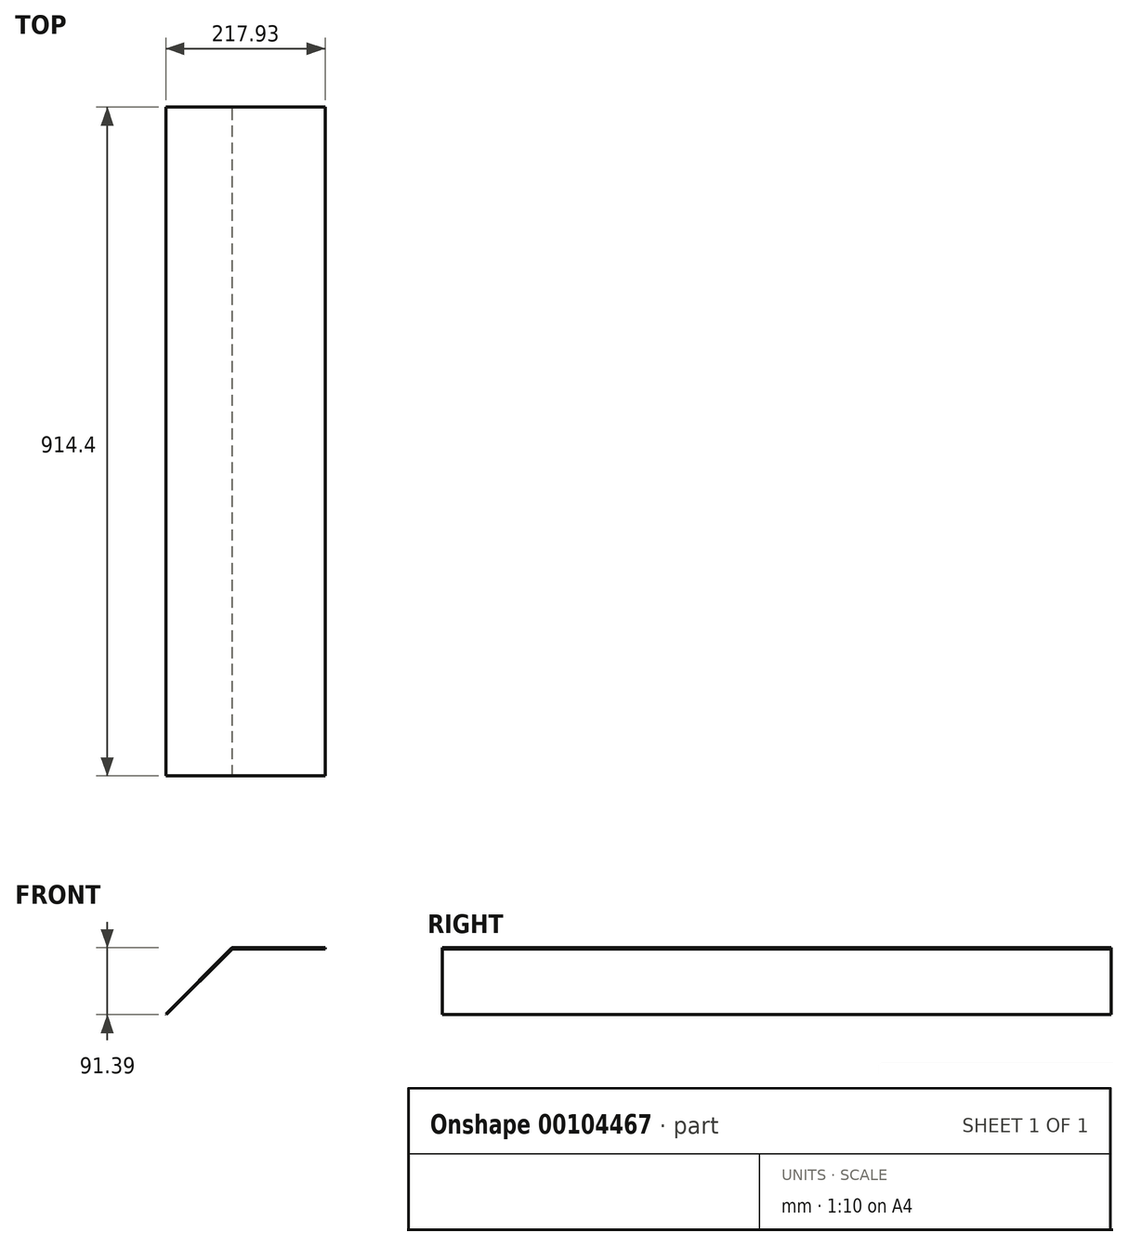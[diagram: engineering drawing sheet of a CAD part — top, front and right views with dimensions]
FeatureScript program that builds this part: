
annotation { "Feature Type Name" : "Feature", "Feature Type Description" : "" }
export const myFeature = defineFeature(function(context is Context, id is Id, definition is map)
    precondition{}
    {
        {
            var Q0;
            Q0=qCreatedBy(makeId("Top.planeOp"),FACE);
            var sketch = newSketch(context, id + "F0", { "sketchPlane" : qUnion([Q0])});
            skLineSegment(sketch, "E0.bottom", {"start": v(0, 0) * mm, "end": v(127, 0) * mm});
            skLineSegment(sketch, "E0.top", {"start": v(0, 914.4) * mm, "end": v(127, 914.4) * mm});
            skLineSegment(sketch, "E0.left", {"start": v(0, 0) * mm, "end": v(0, 914.4) * mm});
            skLineSegment(sketch, "E0.right", {"start": v(127, 0) * mm, "end": v(127, 914.4) * mm});
            skSolve(sketch);
        }
        {
            var Q0;
            Q0 = qSketchRegion(id + "F0", true);
            extrude(context, id + "F1", {"entities" : qUnion([Q0]), "depth" : 1.59 * mm});
        }
        {
            var Q0;
            Q0=qCreatedBy(makeId("Front.planeOp"),FACE);
            var sketch = newSketch(context, id + "F2", { "sketchPlane" : qUnion([Q0])});
            skLineSegment(sketch, "E1", {"start": v(0, 0) * mm, "end": v(-89.8, -89.8) * mm});
            skLineSegment(sketch, "E2", {"start": v(-89.8, -89.8) * mm, "end": v(-90.93, -88.68) * mm});
            skLineSegment(sketch, "E3", {"start": v(-90.93, -88.68) * mm, "end": v(-1.14, 1.1) * mm});
            skArc(sketch, "E4", {"start": v(0, 1.58) * mm, "mid": v(-0.61, 1.46) * mm, "end": v(-1.14, 1.1) * mm});
            skLineSegment(sketch, "E5", {"start": v(0, 1.58) * mm, "end": v(0, 0) * mm});
            skSolve(sketch);
        }
        {
            var Q0;
            Q0 = qSketchRegion(id + "F2", true);
            extrude(context, id + "F3", {"entities" : qUnion([Q0]), "operationType" : NewBodyOperationType.ADD, "oppositeDirection" : true, "depth" : 914.4 * mm});
        }
    });
